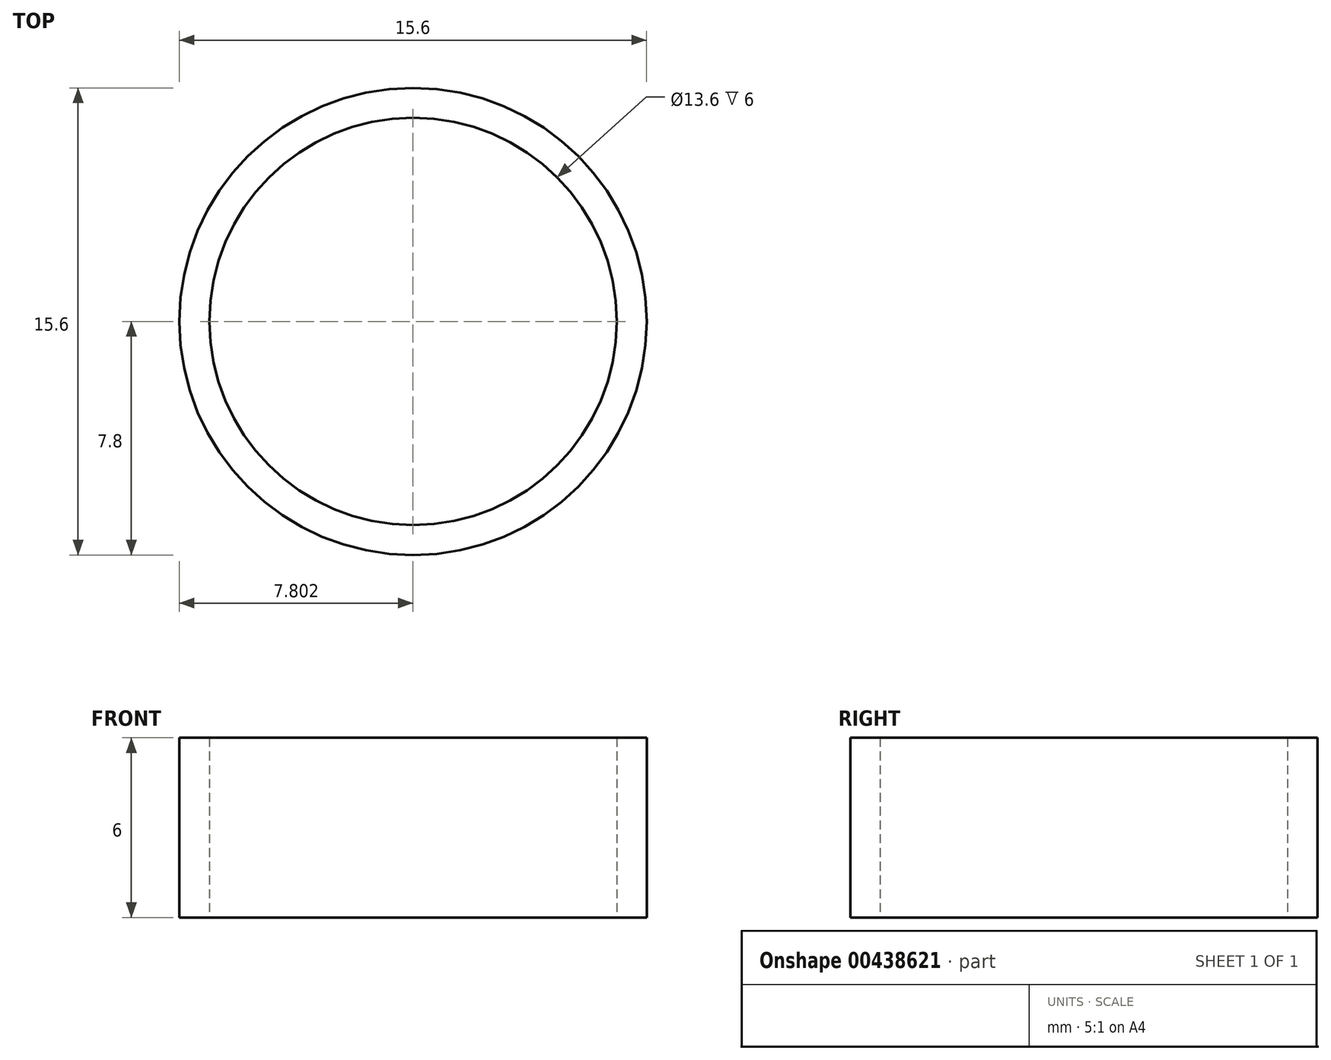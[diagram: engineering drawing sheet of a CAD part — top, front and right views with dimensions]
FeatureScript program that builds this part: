
annotation { "Feature Type Name" : "Feature", "Feature Type Description" : "" }
export const myFeature = defineFeature(function(context is Context, id is Id, definition is map)
    precondition{}
    {
        {
            var Q0;
            Q0=qCreatedBy(makeId("Top.planeOp"),FACE);
            var sketch = newSketch(context, id + "F0", { "sketchPlane" : qUnion([Q0])});
            skCircle(sketch, "E0", {"center": v(0.46, 0) * mm, "radius": 7.8 * mm});
            skCircle(sketch, "E1", {"center": v(0.46, 0) * mm, "radius": 6.8 * mm});
            skSolve(sketch);
        }
        {
            var Q0;
            Q0 = qSketchRegion(id + "F0", true);
            extrude(context, id + "F1", {"entities" : qUnion([Q0]), "depth" : 6 * mm});
        }
    });
